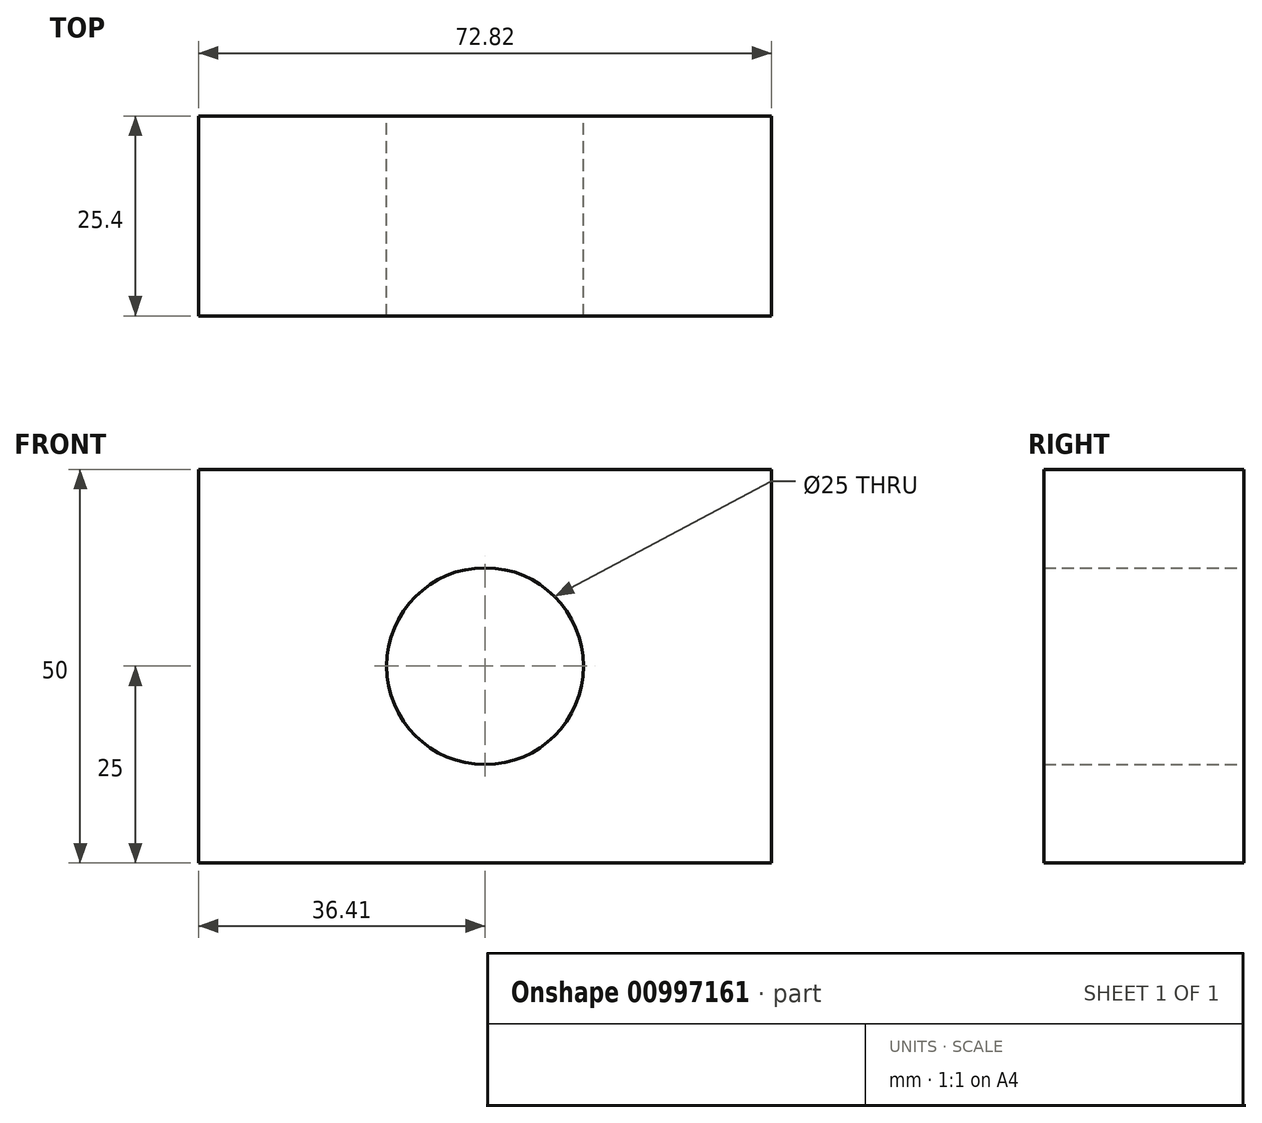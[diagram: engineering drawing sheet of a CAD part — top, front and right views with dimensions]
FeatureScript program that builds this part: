
annotation { "Feature Type Name" : "Feature", "Feature Type Description" : "" }
export const myFeature = defineFeature(function(context is Context, id is Id, definition is map)
    precondition{}
    {
        {
            var Q0;
            Q0=qCreatedBy(makeId("Front.planeOp"),FACE);
            var sketch = newSketch(context, id + "F0", { "sketchPlane" : qUnion([Q0])});
            skLineSegment(sketch, "E0.bottom", {"start": v(36.41, 25) * mm, "end": v(-36.41, 25) * mm});
            skLineSegment(sketch, "E0.top", {"start": v(36.41, -25) * mm, "end": v(-36.41, -25) * mm});
            skLineSegment(sketch, "E0.left", {"start": v(36.41, 25) * mm, "end": v(36.41, -25) * mm});
            skLineSegment(sketch, "E0.right", {"start": v(-36.41, 25) * mm, "end": v(-36.41, -25) * mm});
            skPoint(sketch, "E0.middle", {"position": v(0, 0) * mm});
            skCircle(sketch, "E1", {"center": v(0, 0) * mm, "radius": 12.5 * mm});
            skSolve(sketch);
        }
        {
            var Q0;
            Q0=makeQuery(id+"F0.imprint","IMPRINT",FACE,{"disambiguationData":[TD([[makeQuery(id+"F0.imprint","IMPRINT",EDGE,{"derivedFrom":sQuery(id+"F0.wireOp",EDGE,"E0.bottom")}),1.0]])]});
            extrude(context, id + "F1", {"entities" : qUnion([Q0]), "depth" : 25.4 * mm, "offsetDistance" : 25.4 * mm});
        }
    });
